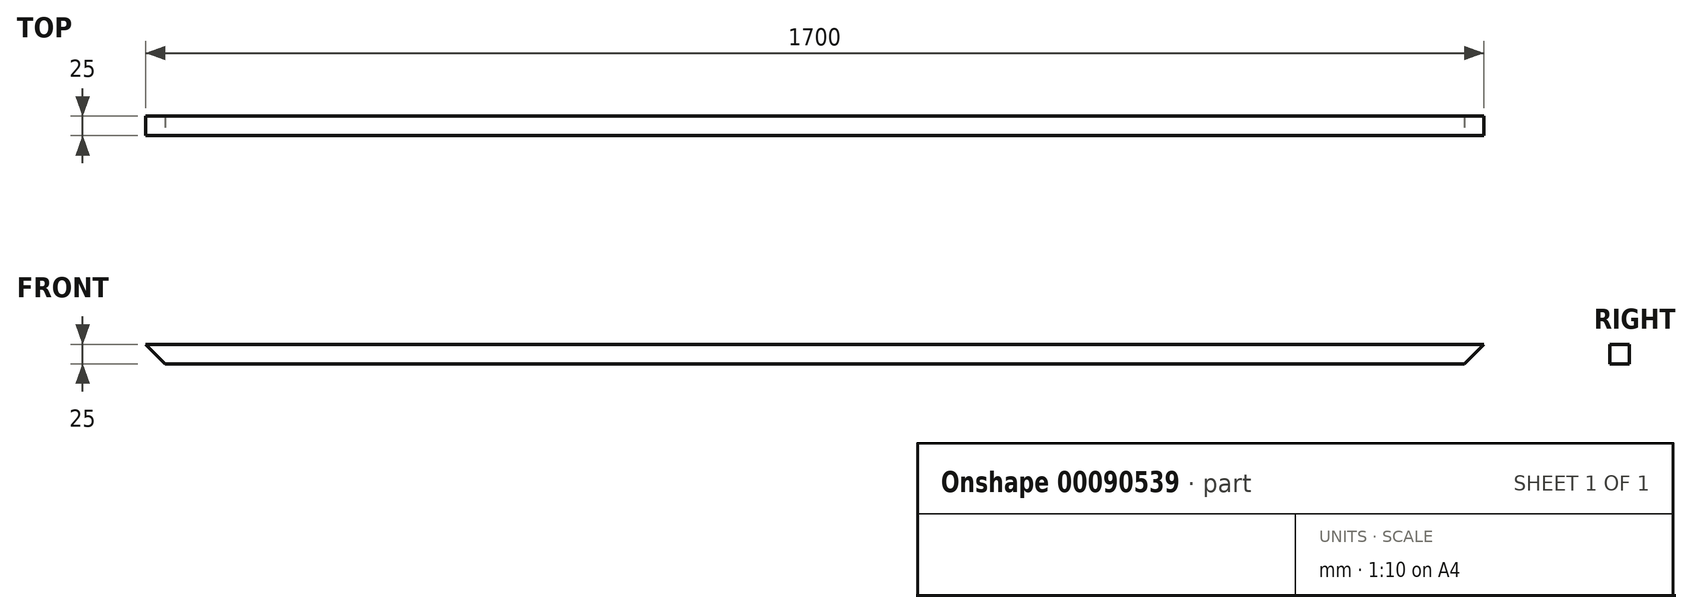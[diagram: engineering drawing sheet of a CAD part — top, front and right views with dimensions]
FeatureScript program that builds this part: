
annotation { "Feature Type Name" : "Feature", "Feature Type Description" : "" }
export const myFeature = defineFeature(function(context is Context, id is Id, definition is map)
    precondition{}
    {
        {
            var Q0;
            Q0=qCreatedBy(makeId("Right.planeOp"),FACE);
            var sketch = newSketch(context, id + "F0", { "sketchPlane" : qUnion([Q0])});
            skLineSegment(sketch, "E0.bottom", {"start": v(12.5, -12.5) * mm, "end": v(-12.5, -12.5) * mm});
            skLineSegment(sketch, "E0.top", {"start": v(12.5, 12.5) * mm, "end": v(-12.5, 12.5) * mm});
            skLineSegment(sketch, "E0.left", {"start": v(12.5, -12.5) * mm, "end": v(12.5, 12.5) * mm});
            skLineSegment(sketch, "E0.right", {"start": v(-12.5, -12.5) * mm, "end": v(-12.5, 12.5) * mm});
            skPoint(sketch, "E0.middle", {"position": v(0, 0) * mm});
            skSolve(sketch);
        }
        {
            var Q0;
            Q0=qSketchRegion(id+"F0",true);
            extrude(context, id + "F1", {"entities" : qUnion([Q0]), "depth" : 1700 * mm});
        }
        {
            var Q0;
            Q0=qCreatedBy(makeId("Front.planeOp"),FACE);
            var sketch = newSketch(context, id + "F2", { "sketchPlane" : qUnion([Q0])});
            skLineSegment(sketch, "E1", {"start": v(0, 12.5) * mm, "end": v(25, -12.5) * mm});
            skLineSegment(sketch, "E2", {"start": v(0, 12.5) * mm, "end": v(0, -12.5) * mm});
            skLineSegment(sketch, "E3", {"start": v(0, -12.5) * mm, "end": v(25, -12.5) * mm});
            skSolve(sketch);
        }
        {
            var Q0;
            Q0=qSketchRegion(id+"F2",true);
            extrude(context, id + "F3", {"entities" : qUnion([Q0]), "operationType" : NewBodyOperationType.REMOVE, "endBound" : BoundingType.THROUGH_ALL, "oppositeDirection" : true, "depth" : 25 * mm, "hasSecondDirection" : true, "secondDirectionBound" : SecondDirectionBoundingType.THROUGH_ALL, "secondDirectionOppositeDirection" : false, "secondDirectionDepth" : 25 * mm});
        }
        {
            var Q0;
            Q0=qCreatedBy(makeId("Front.planeOp"),FACE);
            var sketch = newSketch(context, id + "F4", { "sketchPlane" : qUnion([Q0])});
            skLineSegment(sketch, "E4", {"start": v(1700, 12.5) * mm, "end": v(1675, -12.5) * mm});
            skLineSegment(sketch, "E5", {"start": v(1675, -12.5) * mm, "end": v(1700, -12.5) * mm});
            skLineSegment(sketch, "E6", {"start": v(1700, -12.5) * mm, "end": v(1700, 12.5) * mm});
            skSolve(sketch);
        }
        {
            var Q0;
            Q0=qSketchRegion(id+"F4",true);
            extrude(context, id + "F5", {"entities" : qUnion([Q0]), "operationType" : NewBodyOperationType.REMOVE, "endBound" : BoundingType.THROUGH_ALL, "oppositeDirection" : true, "depth" : 25 * mm, "hasSecondDirection" : true, "secondDirectionBound" : SecondDirectionBoundingType.THROUGH_ALL, "secondDirectionOppositeDirection" : false, "secondDirectionDepth" : 25 * mm});
        }
    });
